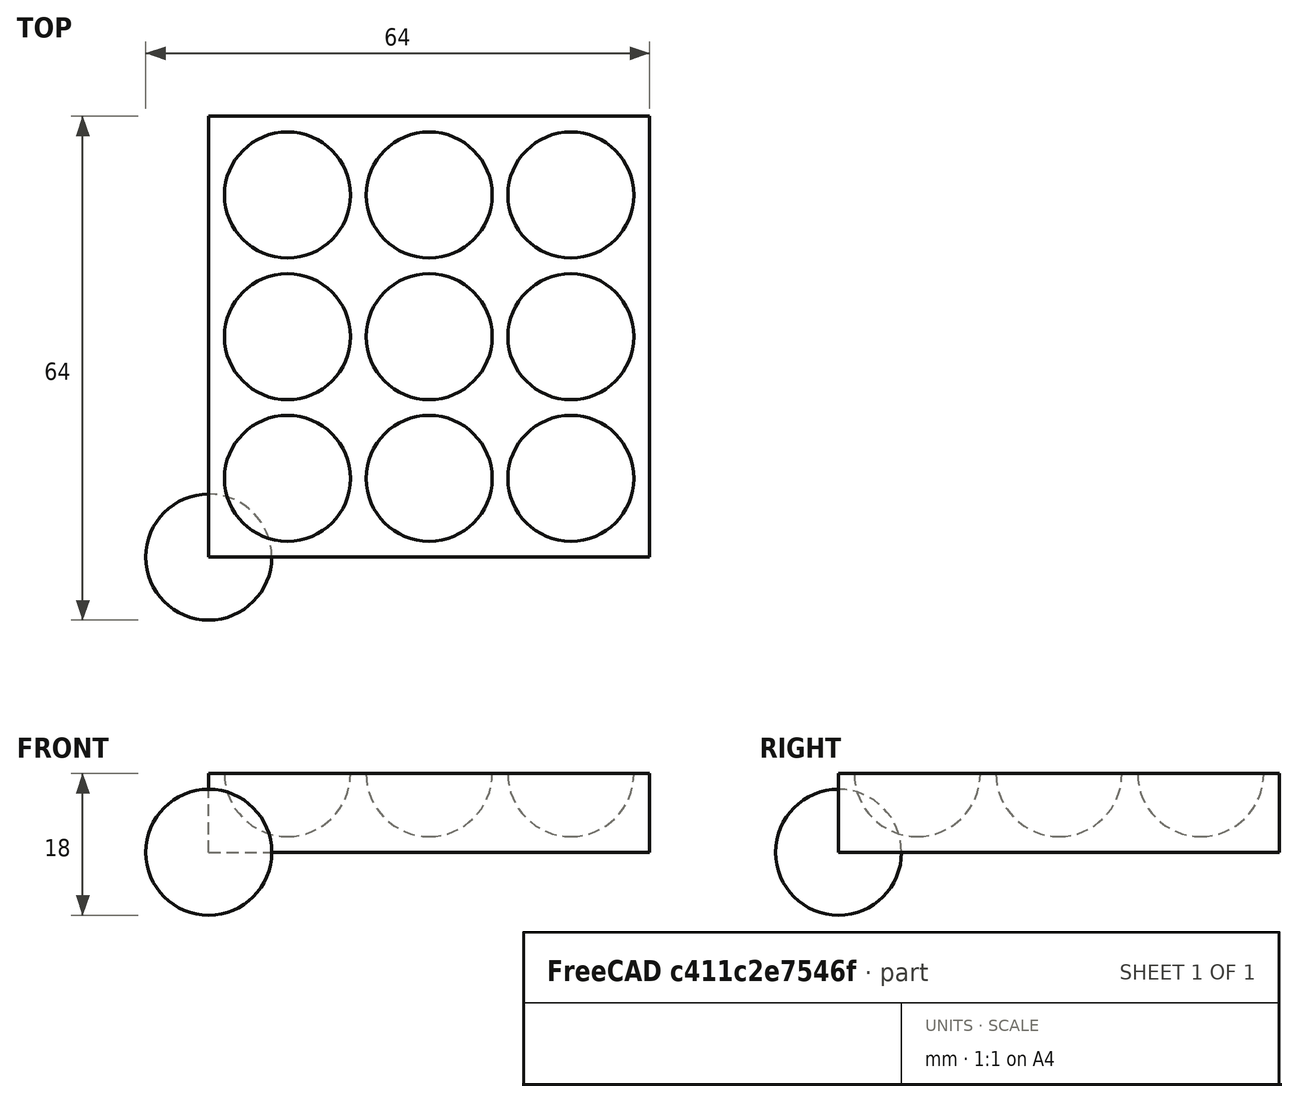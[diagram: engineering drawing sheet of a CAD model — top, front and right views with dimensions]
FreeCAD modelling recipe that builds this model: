
FCSTD DOCUMENT  (FreeCAD 0.21R33694 (Git))
Label: OJT1_T13P01_porta-bales
License: All rights reserved
LicenseURL: https://en.wikipedia.org/wiki/All_rights_reserved
objects: Part::Sphere×1, Part::FeaturePython×1, Part::Box×1, Part::Cut×1
note: 3 computed .brp shape members not serialized (recipe doc carries the construction recipe); baked Part::Feature solids carry a one-line shape summary decoded from their .brp

FEATURE [Part::Sphere] Sphere  label="Esfera"
  Angle1 = -90
  Angle2 = 90
  Angle3 = 360
  AttacherType = Attacher::AttachEngine3D
  Radius = 8
FEATURE [Part::FeaturePython] Array  # Draft array (typed FeaturePython)
  AlwaysSyncPlacement = false
  Angle = 360
  ArrayType = 0
  Axis = (0,0,1)
  Base = -> Sphere
  Center = (0,0,0)
  Count = 9
  ExpandArray = false
  Fuse = false
  IntervalAxis = (0,0,0)
  IntervalX = (18,0,0)
  IntervalY = (0,18,0)
  IntervalZ = (0,0,100)
  NumberCircles = 3
  NumberPolar = 5
  NumberX = 3
  NumberY = 3
  NumberZ = 1
  Placement = pos=(10,10,10) rot=(0,0,1;0rad)
  PlacementList = 9 placements: [(0,0,0),(0,18,0),(0,36,0),(18,0,0),(18,18,0),(18,36,0),(36,0,0),(36,18,0),(36,36,0)]
  RadialDistance = 50
  ScaleList = (9) [(1,1,1),(1,1,1),(1,1,1),(1,1,1),(1,1,1),(1,1,1),(1,1,1),(1,1,1),(1,1,1)]
  Symmetry = 1
  TangentialDistance = 25
FEATURE [Part::Box] Box  label="Cub"
  AttacherType = Attacher::AttachEngine3D
  Height = 10
  Length = 56
  Width = 56
FEATURE [Part::Cut] Cut
  Base = -> Box
  Tool = -> Array
